# Revit family: PANEL
name_source: partatom
category: Lighting Fixtures
units: mm (PartAtom-declared; Revit-internal decimal feet)

## family parameters
Cut with Voids When Loaded = No
Host = Face
Light Source = Yes
Maintain Annotation Orientation = Yes
Part Type = Normal
Room Calculation Point = No
Round Connector Dimension = Use Diameter
Shared = No

## types (3) — shared parameters
Color Filter = 16777215
Default Elevation = 1219 mm
Dimming Lamp Color Temperature Shift = <None>
Emit from Line Length = 610 mm
LuxLight_Alto = 18 mm
LuxLight_AltoAreaLuminosa = 1 mm  [stored 0.00328084 ft]
LuxLight_Ancho = 595 mm
LuxLight_AnchoAreaLuminosa = 595 mm
LuxLight_Largo = 595 mm
LuxLight_LargoAreaLuminosa = 595 mm
LuxLight_Lumenes = 4854 lm
LuxLight_ProtuberanciaTecho = 1 mm  [stored 0.00328084 ft]
LuxLight_Temperatura = 4000 K
LuxLight_Watios = 41 W
Manufacturer = LUXLIGHT
zero-valued in all types: LuxLight_Amperios, LuxLight_Diametro, LuxLight_DiametroAreaLuminosa

## per-type parameters (varying)
| type | Photometric Web File | Tilt Angle |
| LIPANEL 83 | LIPANEL83 .ies | 0.00° |
| LIPANEL 84 | LIPANEL84 .ies | 60.00° |
| LIPANEL 1684 | LIPANEL1684 .ies | 0.00° |

note: [stored X ft] marks values corroborated as IEEE doubles in the binary element streams (Revit-internal decimal feet)

## geometry (parser evidence)
native form markers: Sweep x2
no freeform markers — native parametric forms only
